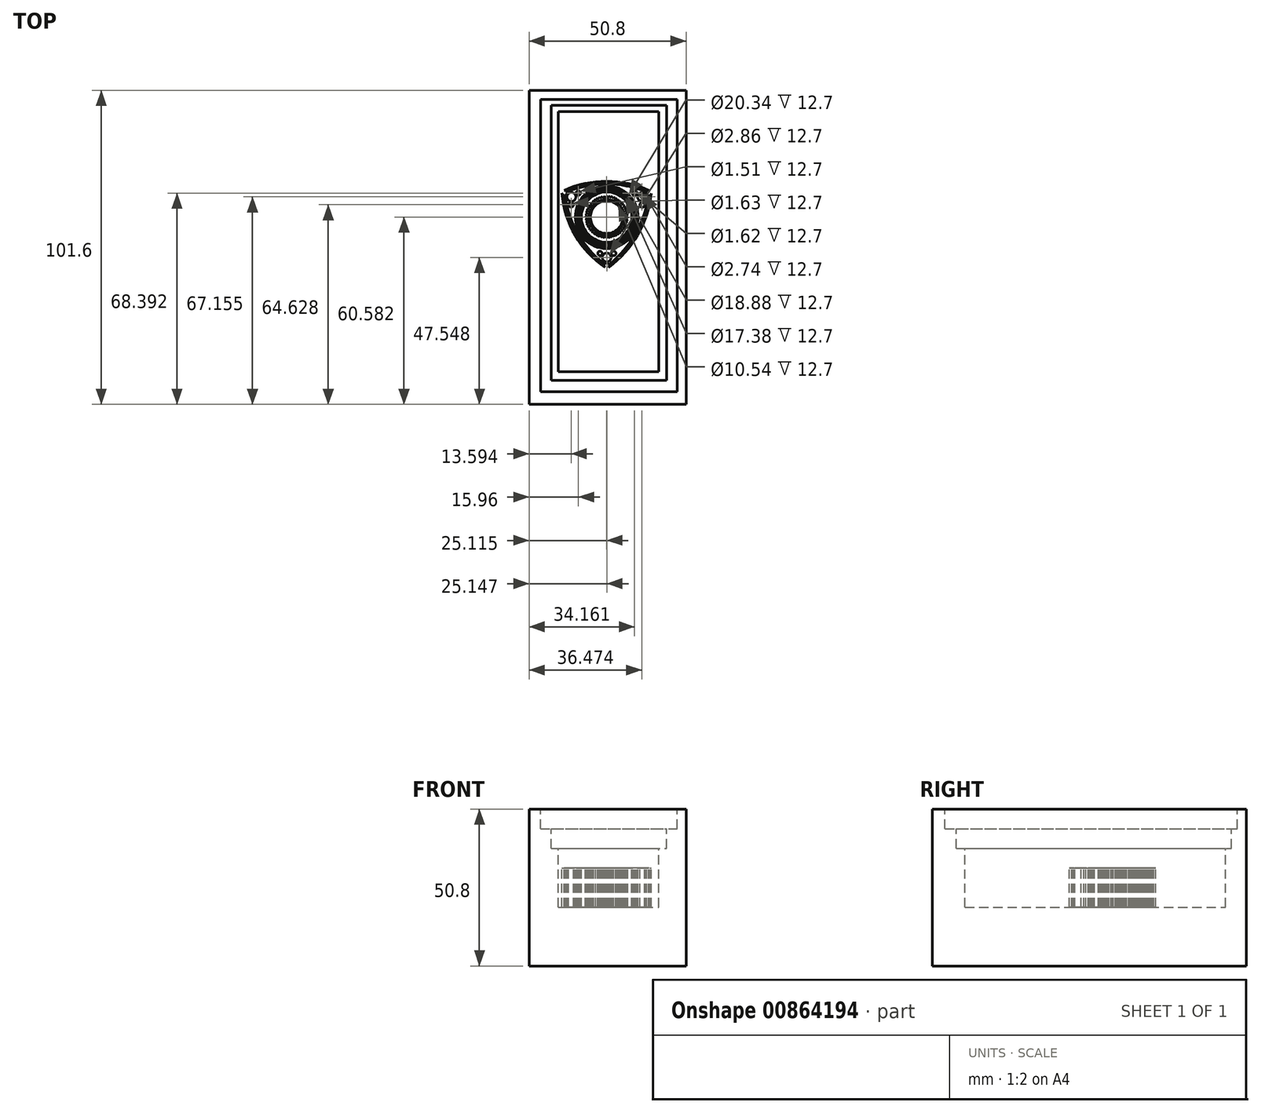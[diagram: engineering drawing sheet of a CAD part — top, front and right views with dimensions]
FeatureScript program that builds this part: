
annotation { "Feature Type Name" : "Feature", "Feature Type Description" : "" }
export const myFeature = defineFeature(function(context is Context, id is Id, definition is map)
    precondition{}
    {
        {
            var Q0;
            Q0=qCreatedBy(makeId("Front.planeOp"),FACE);
            var sketch = newSketch(context, id + "F0", { "sketchPlane" : qUnion([Q0])});
            skLineSegment(sketch, "E0.bottom", {"start": v(-18.63, 16.42) * mm, "end": v(32.17, 16.42) * mm});
            skLineSegment(sketch, "E0.top", {"start": v(-18.63, -34.38) * mm, "end": v(32.17, -34.38) * mm});
            skLineSegment(sketch, "E0.left", {"start": v(-18.63, 16.42) * mm, "end": v(-18.63, -34.38) * mm});
            skLineSegment(sketch, "E0.right", {"start": v(32.17, 16.42) * mm, "end": v(32.17, -34.38) * mm});
            skSolve(sketch);
        }
        {
            var Q0;
            Q0 = qSketchRegion(id + "F0", true);
            extrude(context, id + "F1", {"entities" : qUnion([Q0]), "depth" : 101.6 * mm, "offsetDistance" : 25.4 * mm});
        }
        {
            var Q0;
            Q0=makeQuery(id+"F1.opExtrude","SWEPT_FACE",FACE,{"disambiguationData":[OSD([sQuery(id+"F0.wireOp",EDGE,"E0.bottom")])]});
            var sketch = newSketch(context, id + "F2", { "sketchPlane" : qUnion([Q0])});
            skLineSegment(sketch, "E1.bottom", {"start": v(-14.95, -97.55) * mm, "end": v(29.36, -97.55) * mm});
            skLineSegment(sketch, "E1.top", {"start": v(-14.95, -2.91) * mm, "end": v(29.36, -2.91) * mm});
            skLineSegment(sketch, "E1.left", {"start": v(-14.95, -97.55) * mm, "end": v(-14.95, -2.91) * mm});
            skLineSegment(sketch, "E1.right", {"start": v(29.36, -97.55) * mm, "end": v(29.36, -2.91) * mm});
            skSolve(sketch);
        }
        {
            var Q0;
            Q0=makeQuery(id+"F2.imprint","IMPRINT",FACE,{"disambiguationData":[TD([[makeQuery(id+"F2.imprint","IMPRINT",EDGE,{"derivedFrom":sQuery(id+"F2.wireOp",EDGE,"E1.bottom")}),1.0]])]});
            extrude(context, id + "F3", {"entities" : qUnion([Q0]), "operationType" : NewBodyOperationType.REMOVE, "oppositeDirection" : true, "depth" : 6.35 * mm, "offsetDistance" : 25.4 * mm});
        }
        {
            var Q0;
            Q0=makeQuery(id+"F3.boolean.opBoolean","COPY",FACE,{"derivedFrom":makeQuery(id+"F3.opExtrude","CAP_FACE",FACE,{"disambiguationData":[OSD([sQuery(id+"F2.wireOp",EDGE,"E1.bottom"),sQuery(id+"F2.wireOp",EDGE,"E1.top"),sQuery(id+"F2.wireOp",EDGE,"E1.left"),sQuery(id+"F2.wireOp",EDGE,"E1.right")])],"isStart":false})});
            var sketch = newSketch(context, id + "F4", { "sketchPlane" : qUnion([Q0])});
            skLineSegment(sketch, "E2.bottom", {"start": v(-11.5, -93.9) * mm, "end": v(25.92, -93.9) * mm});
            skLineSegment(sketch, "E2.top", {"start": v(-11.5, -4.85) * mm, "end": v(25.92, -4.85) * mm});
            skLineSegment(sketch, "E2.left", {"start": v(-11.5, -93.9) * mm, "end": v(-11.5, -4.85) * mm});
            skLineSegment(sketch, "E2.right", {"start": v(25.92, -93.9) * mm, "end": v(25.92, -4.85) * mm});
            skSolve(sketch);
        }
        {
            var Q0;
            Q0=makeQuery(id+"F4.imprint","IMPRINT",FACE,{"disambiguationData":[TD([[makeQuery(id+"F4.imprint","IMPRINT",EDGE,{"derivedFrom":sQuery(id+"F4.wireOp",EDGE,"E2.bottom")}),1.0]])]});
            extrude(context, id + "F5", {"entities" : qUnion([Q0]), "operationType" : NewBodyOperationType.REMOVE, "oppositeDirection" : true, "depth" : 6.35 * mm, "offsetDistance" : 25.4 * mm});
        }
        {
            var Q0;
            Q0=makeQuery(id+"F5.boolean.opBoolean","COPY",FACE,{"derivedFrom":makeQuery(id+"F5.opExtrude","CAP_FACE",FACE,{"disambiguationData":[OSD([sQuery(id+"F4.wireOp",EDGE,"E2.bottom"),sQuery(id+"F4.wireOp",EDGE,"E2.top"),sQuery(id+"F4.wireOp",EDGE,"E2.left"),sQuery(id+"F4.wireOp",EDGE,"E2.right")])],"isStart":false})});
            var sketch = newSketch(context, id + "F6", { "sketchPlane" : qUnion([Q0])});
            skLineSegment(sketch, "E3.bottom", {"start": v(-9.14, -91.1) * mm, "end": v(23.34, -91.1) * mm});
            skLineSegment(sketch, "E3.top", {"start": v(-9.14, -6.79) * mm, "end": v(23.34, -6.79) * mm});
            skLineSegment(sketch, "E3.left", {"start": v(-9.14, -91.1) * mm, "end": v(-9.14, -6.79) * mm});
            skLineSegment(sketch, "E3.right", {"start": v(23.34, -91.1) * mm, "end": v(23.34, -6.79) * mm});
            skSolve(sketch);
        }
        {
            var Q0;
            Q0=makeQuery(id+"F6.imprint","IMPRINT",FACE,{"disambiguationData":[TD([[makeQuery(id+"F6.imprint","IMPRINT",EDGE,{"derivedFrom":sQuery(id+"F6.wireOp",EDGE,"E3.bottom")}),1.0]])]});
            extrude(context, id + "F7", {"entities" : qUnion([Q0]), "operationType" : NewBodyOperationType.REMOVE, "oppositeDirection" : true, "depth" : 6.35 * mm, "offsetDistance" : 25.4 * mm});
        }
        {
            var Q0;
            Q0=makeQuery(id+"F7.boolean.opBoolean","COPY",FACE,{"derivedFrom":makeQuery(id+"F7.opExtrude","CAP_FACE",FACE,{"disambiguationData":[OSD([sQuery(id+"F6.wireOp",EDGE,"E3.bottom"),sQuery(id+"F6.wireOp",EDGE,"E3.top"),sQuery(id+"F6.wireOp",EDGE,"E3.left"),sQuery(id+"F6.wireOp",EDGE,"E3.right")])],"isStart":false})});
            var sketch = newSketch(context, id + "F8", { "sketchPlane" : qUnion([Q0])});
            skArc(sketch, "E4", {"start": v(20.16, -32.32) * mm, "mid": v(6.45, -29.37) * mm, "end": v(-7.26, -32.32) * mm});
            skArc(sketch, "E5", {"start": v(7.16, -57.26) * mm, "mid": v(16.53, -46.79) * mm, "end": v(20.87, -33.42) * mm});
            skArc(sketch, "E6", {"start": v(-7.97, -33.26) * mm, "mid": v(-3.73, -46.87) * mm, "end": v(5.97, -57.3) * mm});
            skArc(sketch, "E7", {"start": v(20.63, -32.54) * mm, "mid": v(19.3, -33.54) * mm, "end": v(20.9, -33.08) * mm});
            skArc(sketch, "E8", {"start": v(6.91, -57.44) * mm, "mid": v(6.55, -55.84) * mm, "end": v(6.18, -57.44) * mm});
            skArc(sketch, "E9", {"start": v(-7.98, -33.12) * mm, "mid": v(-6.41, -33.46) * mm, "end": v(-7.7, -32.52) * mm});
            skCircle(sketch, "E10", {"center": v(-4.93, -34.47) * mm, "radius": 1.44 * mm});
            skCircle(sketch, "E11", {"center": v(-2.67, -33.2) * mm, "radius": 0.75 * mm});
            skCircle(sketch, "E12", {"center": v(-5.04, -36.97) * mm, "radius": 0.81 * mm});
            skCircle(sketch, "E13", {"center": v(15.53, -33.2) * mm, "radius": 0.8 * mm});
            skCircle(sketch, "E14", {"center": v(17.84, -34.44) * mm, "radius": 1.37 * mm});
            skCircle(sketch, "E15", {"center": v(17.98, -37.05) * mm, "radius": 0.78 * mm});
            skCircle(sketch, "E16", {"center": v(6.52, -54.05) * mm, "radius": 1.43 * mm});
            skCircle(sketch, "E17", {"center": v(8.76, -52.75) * mm, "radius": 0.76 * mm});
            skCircle(sketch, "E18", {"center": v(4.31, -52.75) * mm, "radius": 0.72 * mm});
            skArc(sketch, "E19", {"start": v(-7.28, -33.94) * mm, "mid": v(-3.1, -46.53) * mm, "end": v(5.75, -56.4) * mm});
            skArc(sketch, "E20", {"start": v(-7, -33.93) * mm, "mid": v(-2.83, -46.37) * mm, "end": v(5.85, -56.2) * mm});
            skArc(sketch, "E21", {"start": v(7.29, -56.28) * mm, "mid": v(15.77, -46.35) * mm, "end": v(20.05, -34.02) * mm});
            skArc(sketch, "E22", {"start": v(7.37, -56.5) * mm, "mid": v(16.1, -46.5) * mm, "end": v(20.37, -33.96) * mm});
            skArc(sketch, "E23", {"start": v(19.3, -32.78) * mm, "mid": v(6.44, -30.31) * mm, "end": v(-6.4, -32.84) * mm});
            skPoint(sketch, "E23.startSnap0", {"position": v(19.3, -33.54) * mm});
            skArc(sketch, "E24", {"start": v(19.44, -32.57) * mm, "mid": v(6.45, -30.04) * mm, "end": v(-6.54, -32.6) * mm});
            skPoint(sketch, "E25", {"position": v(6.48, -30.86) * mm});
            skPoint(sketch, "E26", {"position": v(6.48, -51.12) * mm});
            skPoint(sketch, "E27", {"position": v(16.67, -41.02) * mm});
            skPoint(sketch, "E28", {"position": v(6.48, -41.02) * mm});
            skCircle(sketch, "E29", {"center": v(6.48, -41.02) * mm, "radius": 10.17 * mm});
            skCircle(sketch, "E30", {"center": v(6.48, -41.02) * mm, "radius": 9.77 * mm});
            skCircle(sketch, "E31", {"center": v(6.48, -41.02) * mm, "radius": 9.44 * mm});
            skCircle(sketch, "E32", {"center": v(6.48, -41.02) * mm, "radius": 8.96 * mm});
            skCircle(sketch, "E33", {"center": v(6.48, -41.02) * mm, "radius": 8.7 * mm});
            skCircle(sketch, "E34", {"center": v(6.48, -41.02) * mm, "radius": 8.15 * mm});
            skCircle(sketch, "E35", {"center": v(6.48, -41.02) * mm, "radius": 5.27 * mm});
            skCircle(sketch, "E36", {"center": v(6.48, -41.02) * mm, "radius": 5.74 * mm});
            skLineSegment(sketch, "E37", {"start": v(6.93, -34.13) * mm, "end": v(7.3, -34.64) * mm});
            skLineSegment(sketch, "E38", {"start": v(7.3, -34.64) * mm, "end": v(7.74, -34.2) * mm});
            skLineSegment(sketch, "E39", {"start": v(7.74, -34.2) * mm, "end": v(8.05, -34.81) * mm});
            skLineSegment(sketch, "E40", {"start": v(8.05, -34.81) * mm, "end": v(8.56, -34.43) * mm});
            skLineSegment(sketch, "E41", {"start": v(8.56, -34.43) * mm, "end": v(8.74, -35.04) * mm});
            skLineSegment(sketch, "E42", {"start": v(8.74, -35.04) * mm, "end": v(9.34, -34.7) * mm});
            skLineSegment(sketch, "E43", {"start": v(9.34, -34.7) * mm, "end": v(9.52, -35.36) * mm});
            skLineSegment(sketch, "E44", {"start": v(9.52, -35.36) * mm, "end": v(10.06, -35.1) * mm});
            skLineSegment(sketch, "E45", {"start": v(10.06, -35.1) * mm, "end": v(10.14, -35.76) * mm});
            skLineSegment(sketch, "E46", {"start": v(10.14, -35.76) * mm, "end": v(10.74, -35.67) * mm});
            skLineSegment(sketch, "E47", {"start": v(10.74, -35.67) * mm, "end": v(10.74, -36.28) * mm});
            skLineSegment(sketch, "E48", {"start": v(10.74, -36.28) * mm, "end": v(11.33, -36.14) * mm});
            skLineSegment(sketch, "E49", {"start": v(11.33, -36.14) * mm, "end": v(11.33, -36.82) * mm});
            skLineSegment(sketch, "E50", {"start": v(11.33, -36.82) * mm, "end": v(11.99, -36.82) * mm});
            skLineSegment(sketch, "E51", {"start": v(11.99, -36.82) * mm, "end": v(11.77, -37.35) * mm});
            skLineSegment(sketch, "E52", {"start": v(11.77, -37.35) * mm, "end": v(12.48, -37.35) * mm});
            skLineSegment(sketch, "E53", {"start": v(12.48, -37.35) * mm, "end": v(12.15, -38.08) * mm});
            skLineSegment(sketch, "E54", {"start": v(12.15, -38.08) * mm, "end": v(12.84, -38.16) * mm});
            skLineSegment(sketch, "E55", {"start": v(12.84, -38.16) * mm, "end": v(12.42, -38.77) * mm});
            skLineSegment(sketch, "E56", {"start": v(12.42, -38.77) * mm, "end": v(13.12, -38.93) * mm});
            skLineSegment(sketch, "E57", {"start": v(13.12, -38.93) * mm, "end": v(12.61, -39.51) * mm});
            skLineSegment(sketch, "E58", {"start": v(12.61, -39.51) * mm, "end": v(13.26, -39.8) * mm});
            skLineSegment(sketch, "E59", {"start": v(13.26, -39.8) * mm, "end": v(12.77, -40.24) * mm});
            skLineSegment(sketch, "E60", {"start": v(12.77, -40.24) * mm, "end": v(13.37, -40.6) * mm});
            skLineSegment(sketch, "E61", {"start": v(13.37, -40.6) * mm, "end": v(12.72, -41) * mm});
            skLineSegment(sketch, "E62", {"start": v(12.72, -41) * mm, "end": v(13.36, -41.46) * mm});
            skLineSegment(sketch, "E63", {"start": v(13.36, -41.46) * mm, "end": v(12.77, -41.69) * mm});
            skLineSegment(sketch, "E64", {"start": v(12.77, -41.69) * mm, "end": v(13.26, -42.29) * mm});
            skLineSegment(sketch, "E65", {"start": v(13.26, -42.29) * mm, "end": v(12.53, -42.45) * mm});
            skLineSegment(sketch, "E66", {"start": v(12.53, -42.45) * mm, "end": v(13, -43.08) * mm});
            skLineSegment(sketch, "E67", {"start": v(13, -43.08) * mm, "end": v(12.23, -43.17) * mm});
            skLineSegment(sketch, "E68", {"start": v(12.23, -43.17) * mm, "end": v(12.77, -43.88) * mm});
            skLineSegment(sketch, "E69", {"start": v(12.77, -43.88) * mm, "end": v(12.04, -43.88) * mm});
            skLineSegment(sketch, "E70", {"start": v(12.04, -43.88) * mm, "end": v(12.37, -44.62) * mm});
            skLineSegment(sketch, "E71", {"start": v(12.37, -44.62) * mm, "end": v(11.6, -44.53) * mm});
            skLineSegment(sketch, "E72", {"start": v(11.6, -44.53) * mm, "end": v(11.83, -45.21) * mm});
            skLineSegment(sketch, "E73", {"start": v(11.83, -45.21) * mm, "end": v(11.18, -45.14) * mm});
            skLineSegment(sketch, "E74", {"start": v(11.18, -45.14) * mm, "end": v(11.33, -45.82) * mm});
            skLineSegment(sketch, "E75", {"start": v(11.33, -45.82) * mm, "end": v(10.63, -45.74) * mm});
            skLineSegment(sketch, "E76", {"start": v(10.63, -45.74) * mm, "end": v(10.63, -46.42) * mm});
            skLineSegment(sketch, "E77", {"start": v(10.63, -46.42) * mm, "end": v(10, -46.14) * mm});
            skLineSegment(sketch, "E78", {"start": v(10, -46.14) * mm, "end": v(10, -46.82) * mm});
            skLineSegment(sketch, "E79", {"start": v(10, -46.82) * mm, "end": v(9.33, -46.52) * mm});
            skLineSegment(sketch, "E80", {"start": v(9.33, -46.52) * mm, "end": v(9.33, -47.24) * mm});
            skLineSegment(sketch, "E81", {"start": v(9.33, -47.24) * mm, "end": v(8.7, -46.77) * mm});
            skLineSegment(sketch, "E82", {"start": v(8.7, -46.77) * mm, "end": v(8.37, -47.52) * mm});
            skLineSegment(sketch, "E83", {"start": v(8.37, -47.52) * mm, "end": v(8, -47) * mm});
            skLineSegment(sketch, "E84", {"start": v(8, -47) * mm, "end": v(7.7, -47.68) * mm});
            skLineSegment(sketch, "E85", {"start": v(7.7, -47.68) * mm, "end": v(7.23, -47.08) * mm});
            skLineSegment(sketch, "E86", {"start": v(7.23, -47.08) * mm, "end": v(6.89, -47.85) * mm});
            skLineSegment(sketch, "E87", {"start": v(6.89, -47.85) * mm, "end": v(6.45, -47.17) * mm});
            skLineSegment(sketch, "E88", {"start": v(6.45, -47.17) * mm, "end": v(6.01, -47.77) * mm});
            skLineSegment(sketch, "E89", {"start": v(6.01, -47.77) * mm, "end": v(5.68, -47.14) * mm});
            skLineSegment(sketch, "E90", {"start": v(5.68, -47.14) * mm, "end": v(5.2, -47.8) * mm});
            skLineSegment(sketch, "E91", {"start": v(5.2, -47.8) * mm, "end": v(4.84, -47) * mm});
            skLineSegment(sketch, "E92", {"start": v(4.84, -47) * mm, "end": v(4.47, -47.5) * mm});
            skLineSegment(sketch, "E93", {"start": v(4.47, -47.5) * mm, "end": v(4.24, -46.8) * mm});
            skLineSegment(sketch, "E94", {"start": v(4.24, -46.8) * mm, "end": v(3.58, -47.27) * mm});
            skLineSegment(sketch, "E95", {"start": v(3.58, -47.27) * mm, "end": v(3.52, -46.48) * mm});
            skLineSegment(sketch, "E96", {"start": v(3.52, -46.48) * mm, "end": v(2.86, -46.9) * mm});
            skLineSegment(sketch, "E97", {"start": v(2.86, -46.9) * mm, "end": v(2.84, -46.1) * mm});
            skLineSegment(sketch, "E98", {"start": v(2.84, -46.1) * mm, "end": v(2.15, -46.4) * mm});
            skLineSegment(sketch, "E99", {"start": v(2.15, -46.4) * mm, "end": v(2.24, -45.65) * mm});
            skLineSegment(sketch, "E100", {"start": v(2.24, -45.65) * mm, "end": v(1.52, -45.74) * mm});
            skLineSegment(sketch, "E101", {"start": v(1.52, -45.74) * mm, "end": v(1.8, -45.13) * mm});
            skLineSegment(sketch, "E102", {"start": v(1.8, -45.13) * mm, "end": v(1, -45.24) * mm});
            skLineSegment(sketch, "E103", {"start": v(1, -45.24) * mm, "end": v(1.28, -44.6) * mm});
            skLineSegment(sketch, "E104", {"start": v(1.28, -44.6) * mm, "end": v(0.6, -44.53) * mm});
            skLineSegment(sketch, "E105", {"start": v(0.6, -44.53) * mm, "end": v(0.94, -43.78) * mm});
            skLineSegment(sketch, "E106", {"start": v(0.94, -43.78) * mm, "end": v(0.15, -43.78) * mm});
            skLineSegment(sketch, "E107", {"start": v(0.15, -43.78) * mm, "end": v(0.67, -43.25) * mm});
            skLineSegment(sketch, "E108", {"start": v(0.67, -43.25) * mm, "end": v(-0.1, -43.02) * mm});
            skLineSegment(sketch, "E109", {"start": v(-0.1, -43.02) * mm, "end": v(0.46, -42.42) * mm});
            skLineSegment(sketch, "E110", {"start": v(0.46, -42.42) * mm, "end": v(-0.26, -42.2) * mm});
            skLineSegment(sketch, "E111", {"start": v(-0.26, -42.2) * mm, "end": v(0.34, -41.66) * mm});
            skLineSegment(sketch, "E112", {"start": v(0.34, -41.66) * mm, "end": v(-0.4, -41.33) * mm});
            skLineSegment(sketch, "E113", {"start": v(-0.4, -41.33) * mm, "end": v(0.3, -41.01) * mm});
            skLineSegment(sketch, "E114", {"start": v(0.3, -41.01) * mm, "end": v(-0.45, -40.51) * mm});
            skLineSegment(sketch, "E115", {"start": v(-0.45, -40.51) * mm, "end": v(0.16, -40.19) * mm});
            skLineSegment(sketch, "E116", {"start": v(0.16, -40.19) * mm, "end": v(-0.29, -39.75) * mm});
            skLineSegment(sketch, "E117", {"start": v(-0.29, -39.75) * mm, "end": v(0.3, -39.45) * mm});
            skLineSegment(sketch, "E118", {"start": v(0.3, -39.45) * mm, "end": v(-0.12, -38.9) * mm});
            skLineSegment(sketch, "E119", {"start": v(-0.12, -38.9) * mm, "end": v(0.6, -38.78) * mm});
            skLineSegment(sketch, "E120", {"start": v(0.6, -38.78) * mm, "end": v(0.18, -38.09) * mm});
            skLineSegment(sketch, "E121", {"start": v(0.18, -38.09) * mm, "end": v(0.94, -38.09) * mm});
            skLineSegment(sketch, "E122", {"start": v(0.94, -38.09) * mm, "end": v(0.57, -37.38) * mm});
            skLineSegment(sketch, "E123", {"start": v(0.57, -37.38) * mm, "end": v(1.32, -37.42) * mm});
            skLineSegment(sketch, "E124", {"start": v(1.32, -37.42) * mm, "end": v(1.09, -36.75) * mm});
            skLineSegment(sketch, "E125", {"start": v(1.09, -36.75) * mm, "end": v(1.78, -36.83) * mm});
            skLineSegment(sketch, "E126", {"start": v(1.78, -36.83) * mm, "end": v(1.65, -36.14) * mm});
            skLineSegment(sketch, "E127", {"start": v(1.65, -36.14) * mm, "end": v(2.28, -36.32) * mm});
            skLineSegment(sketch, "E128", {"start": v(2.28, -36.32) * mm, "end": v(2.28, -35.58) * mm});
            skLineSegment(sketch, "E129", {"start": v(2.28, -35.58) * mm, "end": v(2.85, -35.83) * mm});
            skLineSegment(sketch, "E130", {"start": v(2.85, -35.83) * mm, "end": v(2.94, -35.08) * mm});
            skLineSegment(sketch, "E131", {"start": v(2.94, -35.08) * mm, "end": v(3.56, -35.41) * mm});
            skLineSegment(sketch, "E132", {"start": v(3.56, -35.41) * mm, "end": v(3.65, -34.71) * mm});
            skLineSegment(sketch, "E133", {"start": v(3.65, -34.71) * mm, "end": v(4.16, -35.09) * mm});
            skLineSegment(sketch, "E134", {"start": v(4.16, -35.09) * mm, "end": v(4.48, -34.38) * mm});
            skLineSegment(sketch, "E135", {"start": v(4.48, -34.38) * mm, "end": v(4.96, -34.9) * mm});
            skLineSegment(sketch, "E136", {"start": v(4.96, -34.9) * mm, "end": v(5.27, -34.22) * mm});
            skLineSegment(sketch, "E137", {"start": v(5.27, -34.22) * mm, "end": v(5.76, -34.83) * mm});
            skLineSegment(sketch, "E138", {"start": v(5.76, -34.83) * mm, "end": v(6.1, -34.16) * mm});
            skLineSegment(sketch, "E139", {"start": v(6.1, -34.16) * mm, "end": v(6.48, -34.79) * mm});
            skLineSegment(sketch, "E140", {"start": v(6.48, -34.79) * mm, "end": v(6.93, -34.13) * mm});
            skLineSegment(sketch, "E141.bottom", {"start": v(-9.14, -6.79) * mm, "end": v(23.34, -6.79) * mm});
            skLineSegment(sketch, "E141.top", {"start": v(-9.14, -91.1) * mm, "end": v(23.34, -91.1) * mm});
            skLineSegment(sketch, "E141.left", {"start": v(-9.14, -6.79) * mm, "end": v(-9.14, -91.1) * mm});
            skLineSegment(sketch, "E141.right", {"start": v(23.34, -6.79) * mm, "end": v(23.34, -91.1) * mm});
            skSolve(sketch);
        }
        {
            var Q0;
            {var subQ13=sQuery(id+"F8.wireOp",EDGE,"E4");Q0=makeQuery(id+"F8.imprint","IMPRINT",FACE,{"disambiguationData":[TD([[makeQuery(id+"F8.imprint","IMPRINT",EDGE,{"derivedFrom":subQ13}),-1.0]])]});}
            var Q1;
            Q1=makeQuery(id+"F8.imprint","IMPRINT",FACE,{"disambiguationData":[TD([[makeQuery(id+"F8.imprint","IMPRINT",EDGE,{"derivedFrom":sQuery(id+"F8.wireOp",EDGE,"E16")}),1.0]])]});
            var Q2;
            Q2=makeQuery(id+"F8.imprint","IMPRINT",FACE,{"disambiguationData":[TD([[makeQuery(id+"F8.imprint","IMPRINT",EDGE,{"derivedFrom":sQuery(id+"F8.wireOp",EDGE,"E18")}),1.0]])]});
            var Q3;
            Q3=makeQuery(id+"F8.imprint","IMPRINT",FACE,{"disambiguationData":[TD([[makeQuery(id+"F8.imprint","IMPRINT",EDGE,{"derivedFrom":sQuery(id+"F8.wireOp",EDGE,"E17")}),1.0]])]});
            var Q4;
            {var subQ0=sQuery(id+"F8.wireOp",EDGE,"E19");Q4=makeQuery(id+"F8.imprint","IMPRINT",FACE,{"disambiguationData":[TD([[makeQuery(id+"F8.imprint","IMPRINT",EDGE,{"derivedFrom":subQ0}),1.0]])]});}
            var Q5;
            {var subQ0=sQuery(id+"F8.wireOp",EDGE,"E21");Q5=makeQuery(id+"F8.imprint","IMPRINT",FACE,{"disambiguationData":[TD([[makeQuery(id+"F8.imprint","IMPRINT",EDGE,{"derivedFrom":subQ0}),-1.0]])]});}
            var Q6;
            {var subQ0=sQuery(id+"F8.wireOp",EDGE,"E23");Q6=makeQuery(id+"F8.imprint","IMPRINT",FACE,{"disambiguationData":[TD([[makeQuery(id+"F8.imprint","IMPRINT",EDGE,{"derivedFrom":subQ0}),-1.0]])]});}
            var Q7;
            Q7=makeQuery(id+"F8.imprint","IMPRINT",FACE,{"disambiguationData":[TD([[makeQuery(id+"F8.imprint","IMPRINT",EDGE,{"derivedFrom":sQuery(id+"F8.wireOp",EDGE,"E10")}),1.0]])]});
            var Q8;
            Q8=makeQuery(id+"F8.imprint","IMPRINT",FACE,{"disambiguationData":[TD([[makeQuery(id+"F8.imprint","IMPRINT",EDGE,{"derivedFrom":sQuery(id+"F8.wireOp",EDGE,"E11")}),1.0]])]});
            var Q9;
            Q9=makeQuery(id+"F8.imprint","IMPRINT",FACE,{"disambiguationData":[TD([[makeQuery(id+"F8.imprint","IMPRINT",EDGE,{"derivedFrom":sQuery(id+"F8.wireOp",EDGE,"E12")}),1.0]])]});
            var Q10;
            Q10=makeQuery(id+"F8.imprint","IMPRINT",FACE,{"disambiguationData":[TD([[makeQuery(id+"F8.imprint","IMPRINT",EDGE,{"derivedFrom":sQuery(id+"F8.wireOp",EDGE,"E13")}),1.0]])]});
            var Q11;
            Q11=makeQuery(id+"F8.imprint","IMPRINT",FACE,{"disambiguationData":[TD([[makeQuery(id+"F8.imprint","IMPRINT",EDGE,{"derivedFrom":sQuery(id+"F8.wireOp",EDGE,"E14")}),1.0]])]});
            var Q12;
            Q12=makeQuery(id+"F8.imprint","IMPRINT",FACE,{"disambiguationData":[TD([[makeQuery(id+"F8.imprint","IMPRINT",EDGE,{"derivedFrom":sQuery(id+"F8.wireOp",EDGE,"E35")}),1.0]])]});
            var Q13;
            Q13=makeQuery(id+"F8.imprint","IMPRINT",FACE,{"disambiguationData":[TD([[makeQuery(id+"F8.imprint","IMPRINT",EDGE,{"derivedFrom":sQuery(id+"F8.wireOp",EDGE,"E36")}),-1.0]])]});
            var Q14;
            Q14=makeQuery(id+"F8.imprint","IMPRINT",FACE,{"disambiguationData":[TD([[makeQuery(id+"F8.imprint","IMPRINT",EDGE,{"derivedFrom":sQuery(id+"F8.wireOp",EDGE,"E33")}),1.0]])]});
            var Q15;
            Q15=makeQuery(id+"F8.imprint","IMPRINT",FACE,{"disambiguationData":[TD([[makeQuery(id+"F8.imprint","IMPRINT",EDGE,{"derivedFrom":sQuery(id+"F8.wireOp",EDGE,"E31")}),1.0]])]});
            var Q16;
            Q16=makeQuery(id+"F8.imprint","IMPRINT",FACE,{"disambiguationData":[TD([[makeQuery(id+"F8.imprint","IMPRINT",EDGE,{"derivedFrom":sQuery(id+"F8.wireOp",EDGE,"E29")}),1.0]])]});
            var Q17;
            Q17=makeQuery(id+"F8.imprint","IMPRINT",FACE,{"disambiguationData":[TD([[makeQuery(id+"F8.imprint","IMPRINT",EDGE,{"derivedFrom":sQuery(id+"F8.wireOp",EDGE,"E15")}),1.0]])]});
            extrude(context, id + "F9", {"entities" : qUnion([Q0, Q1, Q2, Q3, Q4, Q5, Q6, Q7, Q8, Q9, Q10, Q11, Q12, Q13, Q14, Q15, Q16, Q17]), "operationType" : NewBodyOperationType.REMOVE, "oppositeDirection" : true, "depth" : 12.7 * mm, "offsetDistance" : 25.4 * mm});
        }
    });
